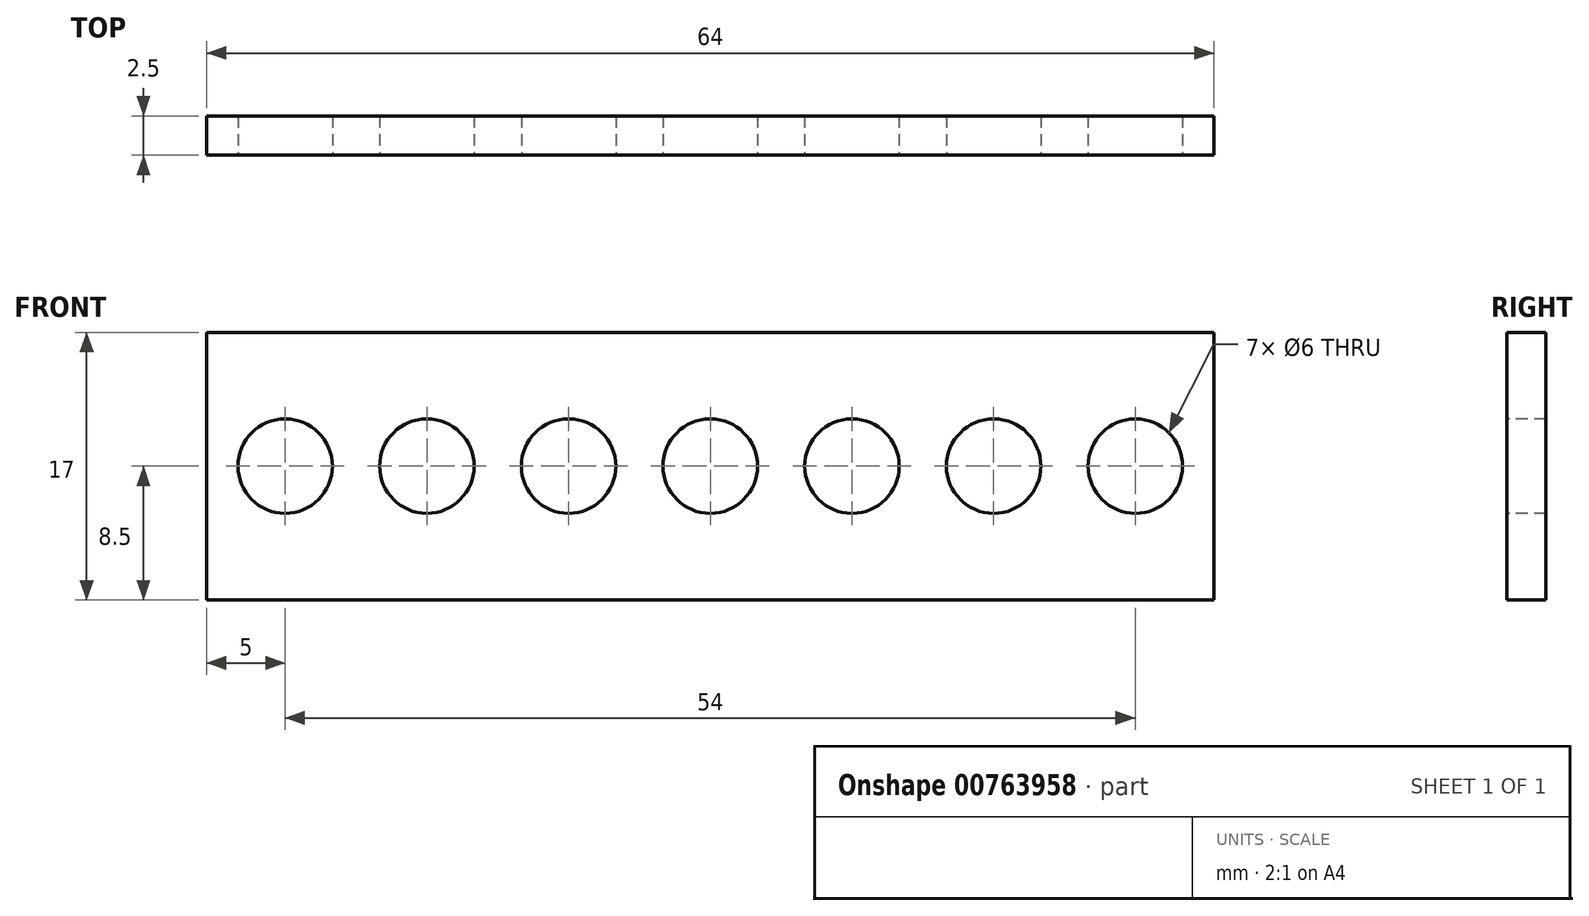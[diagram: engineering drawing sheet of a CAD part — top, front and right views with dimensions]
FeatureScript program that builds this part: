
annotation { "Feature Type Name" : "Feature", "Feature Type Description" : "" }
export const myFeature = defineFeature(function(context is Context, id is Id, definition is map)
    precondition{}
    {
        {
            var Q0;
            Q0=qCreatedBy(makeId("Front.planeOp"),FACE);
            var sketch = newSketch(context, id + "F0", { "sketchPlane" : qUnion([Q0])});
            skLineSegment(sketch, "E0.bottom", {"start": v(32, -8.5) * mm, "end": v(-32, -8.5) * mm});
            skLineSegment(sketch, "E0.top", {"start": v(32, 8.5) * mm, "end": v(-32, 8.5) * mm});
            skLineSegment(sketch, "E0.left", {"start": v(32, -8.5) * mm, "end": v(32, 8.5) * mm});
            skLineSegment(sketch, "E0.right", {"start": v(-32, -8.5) * mm, "end": v(-32, 8.5) * mm});
            skPoint(sketch, "E0.middle", {"position": v(0, 0) * mm});
            skSolve(sketch);
        }
        {
            var Q0;
            Q0=makeQuery(id+"F0.imprint","IMPRINT",FACE,{"disambiguationData":[TD([[makeQuery(id+"F0.imprint","IMPRINT",EDGE,{"derivedFrom":sQuery(id+"F0.wireOp",EDGE,"E0.bottom")}),-1.0]])]});
            extrude(context, id + "F1", {"entities" : qUnion([Q0]), "depth" : 2.5 * mm, "offsetDistance" : 25 * mm});
        }
        {
            var Q0;
            Q0=makeQuery(id+"F1.opExtrude","CAP_FACE",FACE,{"disambiguationData":[OSD([sQuery(id+"F0.wireOp",EDGE,"E0.bottom"),sQuery(id+"F0.wireOp",EDGE,"E0.top"),sQuery(id+"F0.wireOp",EDGE,"E0.left"),sQuery(id+"F0.wireOp",EDGE,"E0.right")])],"isStart":false});
            var sketch = newSketch(context, id + "F2", { "sketchPlane" : qUnion([Q0])});
            skCircle(sketch, "E1", {"center": v(27, 0) * mm, "radius": 3 * mm});
            skCircle(sketch, "E2", {"center": v(18, 0) * mm, "radius": 3 * mm});
            skPoint(sketch, "E2.centerSnap0", {"position": v(32, 0) * mm});
            skCircle(sketch, "E3", {"center": v(9, 0) * mm, "radius": 3 * mm});
            skCircle(sketch, "E4", {"center": v(0, 0) * mm, "radius": 3 * mm});
            skCircle(sketch, "E5", {"center": v(-9, 0) * mm, "radius": 3 * mm});
            skCircle(sketch, "E6", {"center": v(-18, 0) * mm, "radius": 3 * mm});
            skCircle(sketch, "E7", {"center": v(-27, 0) * mm, "radius": 3 * mm});
            skSolve(sketch);
        }
        {
            var Q0;
            Q0 = qSketchRegion(id + "F2", true);
            extrude(context, id + "F3", {"entities" : qUnion([Q0]), "operationType" : NewBodyOperationType.REMOVE, "endBound" : BoundingType.THROUGH_ALL, "oppositeDirection" : true, "depth" : 25 * mm, "offsetDistance" : 25 * mm});
        }
    });
